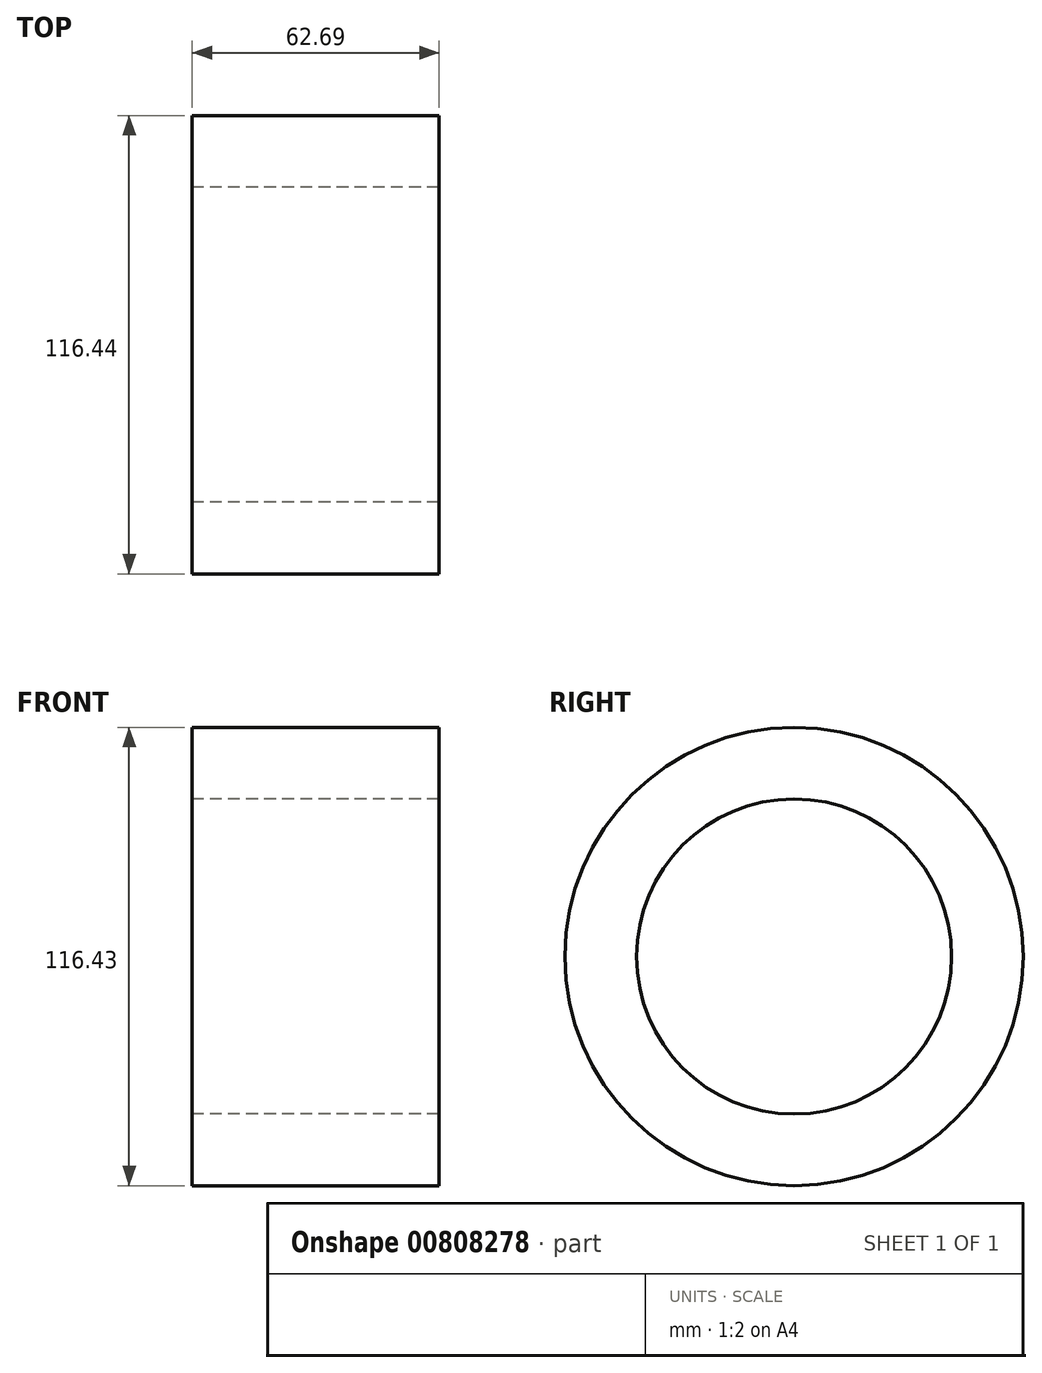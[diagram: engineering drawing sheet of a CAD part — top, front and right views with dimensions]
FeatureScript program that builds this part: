
annotation { "Feature Type Name" : "Feature", "Feature Type Description" : "" }
export const myFeature = defineFeature(function(context is Context, id is Id, definition is map)
    precondition{}
    {
        {
            var Q0;
            Q0=qCreatedBy(makeId("Front.planeOp"),FACE);
            var sketch = newSketch(context, id + "F0", { "sketchPlane" : qUnion([Q0])});
            skLineSegment(sketch, "E0.bottom", {"start": v(-32.87, -28.11) * mm, "end": v(29.82, -28.11) * mm});
            skLineSegment(sketch, "E0.top", {"start": v(-32.87, 30.1) * mm, "end": v(29.82, 30.1) * mm});
            skLineSegment(sketch, "E0.left", {"start": v(-32.87, -28.11) * mm, "end": v(-32.87, 30.1) * mm});
            skLineSegment(sketch, "E0.right", {"start": v(29.82, -28.11) * mm, "end": v(29.82, 30.1) * mm});
            skLineSegment(sketch, "E1", {"start": v(-32.87, -9.92) * mm, "end": v(29.82, -9.92) * mm});
            skSolve(sketch);
        }
        {
            var Q0;
            {var subQ0=sQuery(id+"F0.wireOp",EDGE,"E0.bottom");Q0=makeQuery(id+"F0.imprint","IMPRINT",FACE,{"disambiguationData":[TD([[makeQuery(id+"F0.imprint","IMPRINT",EDGE,{"derivedFrom":subQ0}),1.0]])]});}
            var Q1;
            Q1=sQuery(id+"F0.wireOp",EDGE,"E0.top");
            revolve(context, id + "F1", {"surfaceOperationType" : NewSurfaceOperationType.NEW, "entities" : qUnion([Q0]), "axis" : qUnion([Q1]), "revolveType" : RevolveType.FULL});
        }
    });
